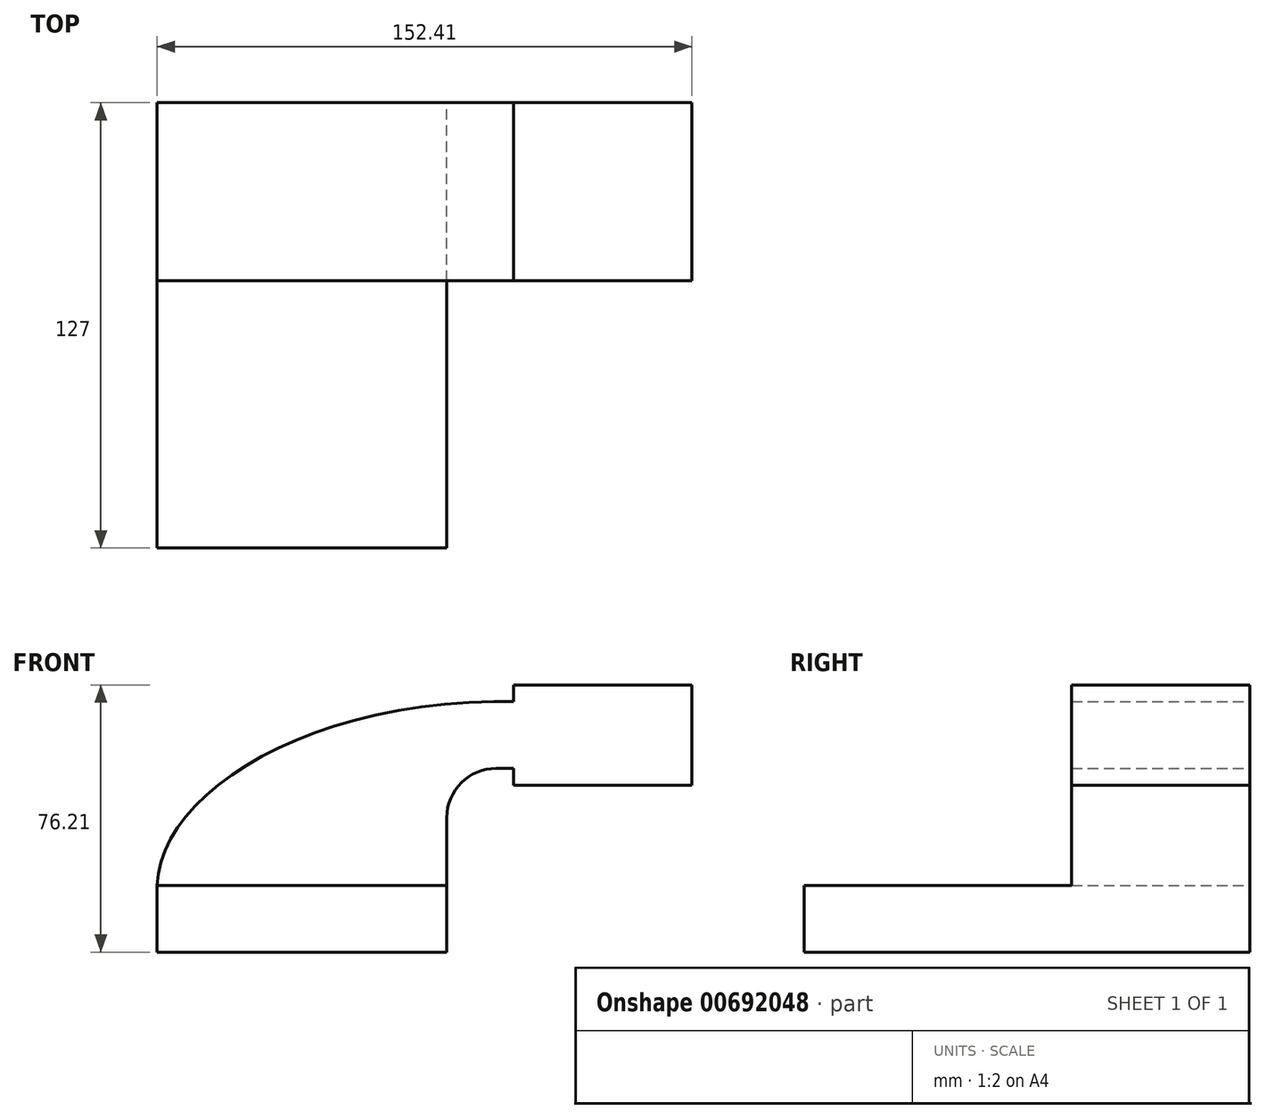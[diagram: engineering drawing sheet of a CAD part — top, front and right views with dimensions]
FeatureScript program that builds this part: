
annotation { "Feature Type Name" : "Feature", "Feature Type Description" : "" }
export const myFeature = defineFeature(function(context is Context, id is Id, definition is map)
    precondition{}
    {
        {
            var Q0;
            Q0=qCreatedBy(makeId("Front.planeOp"),FACE);
            var sketch = newSketch(context, id + "F0", { "sketchPlane" : qUnion([Q0])});
            skLineSegment(sketch, "E0.bottom", {"start": v(41.28, -9.52) * mm, "end": v(-41.28, -9.53) * mm});
            skLineSegment(sketch, "E0.top", {"start": v(41.27, 9.53) * mm, "end": v(-41.28, 9.53) * mm});
            skLineSegment(sketch, "E0.left", {"start": v(41.28, -9.52) * mm, "end": v(41.28, 9.53) * mm});
            skLineSegment(sketch, "E0.right", {"start": v(-41.28, -9.53) * mm, "end": v(-41.28, 9.53) * mm});
            skPoint(sketch, "E0.middle", {"position": v(0, 0) * mm});
            skLineSegment(sketch, "E1.bottom", {"start": v(111.12, 38.1) * mm, "end": v(60.32, 38.1) * mm});
            skLineSegment(sketch, "E1.top", {"start": v(111.12, 66.68) * mm, "end": v(60.32, 66.68) * mm});
            skLineSegment(sketch, "E1.left", {"start": v(111.12, 38.1) * mm, "end": v(111.12, 66.68) * mm});
            skLineSegment(sketch, "E1.right", {"start": v(60.32, 38.1) * mm, "end": v(60.32, 66.68) * mm});
            skPoint(sketch, "E1.middle", {"position": v(85.72, 52.39) * mm});
            skLineSegment(sketch, "E2", {"start": v(41.27, 9.53) * mm, "end": v(41.27, 28.8) * mm});
            skArc(sketch, "E3", {"start": v(41.27, 28.8) * mm, "mid": v(45.4, 38.75) * mm, "end": v(55.36, 42.88) * mm});
            skLineSegment(sketch, "E4", {"start": v(55.36, 42.88) * mm, "end": v(85.72, 42.88) * mm});
            skLineSegment(sketch, "E5.0", {"start": v(55.36, 61.93) * mm, "end": v(85.72, 61.93) * mm});
            skArc(sketch, "E5.1", {"start": v(22.22, 28.8) * mm, "mid": v(31.93, 52.22) * mm, "end": v(55.36, 61.93) * mm});
            skLineSegment(sketch, "E5.2", {"start": v(22.22, 9.53) * mm, "end": v(22.22, 28.8) * mm});
            skLineSegment(sketch, "E6", {"start": v(85.72, 38.1) * mm, "end": v(85.72, 66.68) * mm});
            skFitSpline(sketch, "E7", {"points": [v(-41.28, 9.53) * mm, v(55.36, 61.93) * mm], "startDerivative": vector(1.97, 76.28) * mm, "endDerivative": vector(166.07, 1.33) * mm});
            skSolve(sketch);
        }
        {
            var Q0;
            Q0=makeQuery(id+"F0.imprint","IMPRINT",FACE,{"disambiguationData":[TD([[makeQuery(id+"F0.imprint","IMPRINT",EDGE,{"derivedFrom":sQuery(id+"F0.wireOp",EDGE,"E0.bottom")}),-1.0]])]});
            extrude(context, id + "F1", {"entities" : qUnion([Q0]), "depth" : 127 * mm, "offsetDistance" : 25.4 * mm});
        }
        {
            var Q0;
            Q0 = qSketchRegion(id + "F0", true);
            extrude(context, id + "F2", {"entities" : qUnion([Q0]), "operationType" : NewBodyOperationType.ADD, "depth" : 50.8 * mm, "offsetDistance" : 25.4 * mm});
        }
    });
